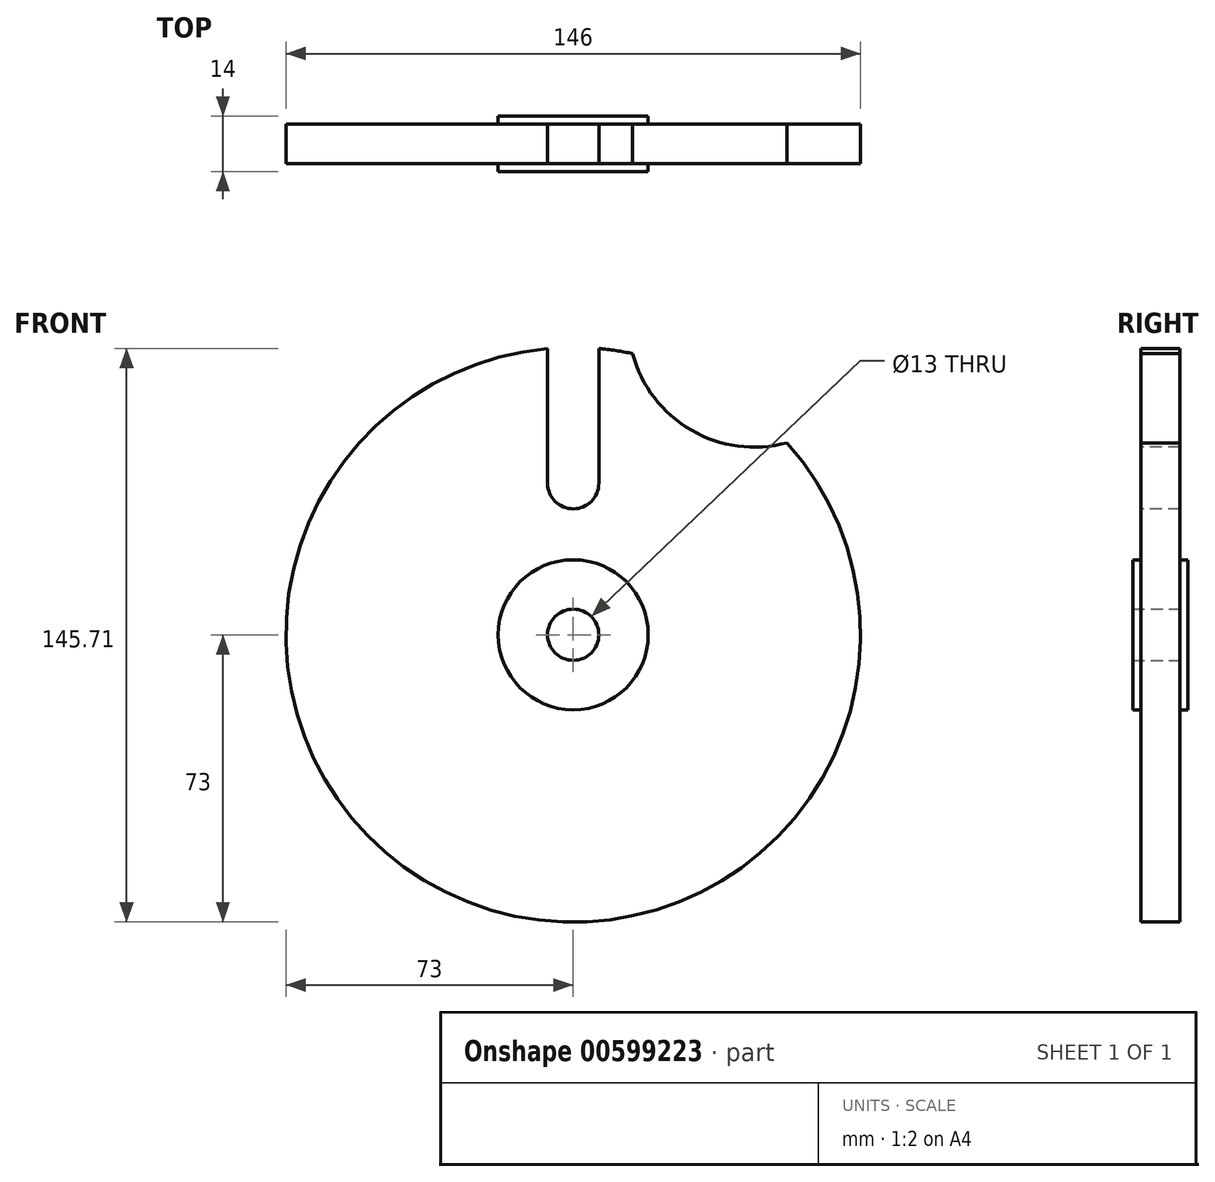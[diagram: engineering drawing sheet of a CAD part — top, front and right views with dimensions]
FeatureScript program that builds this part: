
annotation { "Feature Type Name" : "Feature", "Feature Type Description" : "" }
export const myFeature = defineFeature(function(context is Context, id is Id, definition is map)
    precondition{}
    {
        {
            var Q0;
            Q0=qCreatedBy(makeId("Front.planeOp"),FACE);
            var sketch = newSketch(context, id + "F0", { "sketchPlane" : qUnion([Q0])});
            skCircle(sketch, "E0", {"center": v(0, 92) * mm, "radius": 6.35 * mm, "construction": true});
            skCircle(sketch, "E1", {"center": v(0, 92) * mm, "radius": 31.75 * mm, "construction": true});
            skCircle(sketch, "E2", {"center": v(0, 0) * mm, "radius": 73 * mm, "construction": true});
            skLineSegment(sketch, "E3", {"start": v(0, 0) * mm, "end": v(36.5, 63.22) * mm, "construction": true});
            skCircle(sketch, "E4", {"center": v(0, 38.5) * mm, "radius": 6.35 * mm, "construction": true});
            skSolve(sketch);
        }
        {
            var Q0;
            Q0=qCreatedBy(makeId("Front.planeOp"),FACE);
            var sketch = newSketch(context, id + "F1", { "sketchPlane" : qUnion([Q0])});
            skCircle(sketch, "E5", {"center": v(0, 0) * mm, "radius": 73 * mm});
            skSolve(sketch);
        }
        {
            var Q0;
            Q0 = qSketchRegion(id + "F1", true);
            extrude(context, id + "F2", {"entities" : qUnion([Q0]), "endBound" : BoundingType.SYMMETRIC, "depth" : 10 * mm, "offsetDistance" : 25 * mm});
        }
        {
            var Q0;
            Q0=qCreatedBy(makeId("Front.planeOp"),FACE);
            var sketch = newSketch(context, id + "F3", { "sketchPlane" : qUnion([Q0])});
            skArc(sketch, "E6", {"start": v(-6.5, 38.5) * mm, "mid": v(0, 32) * mm, "end": v(6.5, 38.5) * mm});
            skLineSegment(sketch, "E7", {"start": v(-6.5, 38.5) * mm, "end": v(-6.5, 95.54) * mm});
            skLineSegment(sketch, "E8", {"start": v(-6.5, 95.54) * mm, "end": v(6.5, 95.54) * mm});
            skLineSegment(sketch, "E9", {"start": v(6.5, 38.5) * mm, "end": v(6.5, 95.54) * mm});
            skSolve(sketch);
        }
        {
            var Q0;
            Q0 = qSketchRegion(id + "F3", true);
            extrude(context, id + "F4", {"entities" : qUnion([Q0]), "operationType" : NewBodyOperationType.REMOVE, "endBound" : BoundingType.THROUGH_ALL, "oppositeDirection" : true, "depth" : 25 * mm, "offsetDistance" : 25 * mm, "hasSecondDirection" : true, "secondDirectionBound" : SecondDirectionBoundingType.THROUGH_ALL, "secondDirectionOppositeDirection" : false, "secondDirectionDepth" : 25 * mm});
        }
        {
            var Q0;
            Q0=qCreatedBy(makeId("Right.planeOp"),FACE);
            var sketch = newSketch(context, id + "F5", { "sketchPlane" : qUnion([Q0])});
            skLineSegment(sketch, "E10", {"start": v(10, 0) * mm, "end": v(-10, 0) * mm, "construction": true});
            skSolve(sketch);
        }
        {
            var Q0;
            Q0=qCreatedBy(makeId("Front.planeOp"),FACE);
            var sketch = newSketch(context, id + "F6", { "sketchPlane" : qUnion([Q0])});
            skCircle(sketch, "E11", {"center": v(0, 0) * mm, "radius": 92 * mm, "construction": true});
            skCircle(sketch, "E12", {"center": v(46, 79.67) * mm, "radius": 32 * mm});
            skSolve(sketch);
        }
        {
            var Q0;
            Q0 = qSketchRegion(id + "F6", true);
            extrude(context, id + "F7", {"entities" : qUnion([Q0]), "operationType" : NewBodyOperationType.REMOVE, "endBound" : BoundingType.THROUGH_ALL, "oppositeDirection" : true, "depth" : 25 * mm, "offsetDistance" : 25 * mm, "hasSecondDirection" : true, "secondDirectionBound" : SecondDirectionBoundingType.THROUGH_ALL, "secondDirectionOppositeDirection" : false, "secondDirectionDepth" : 25 * mm});
        }
        {
            var Q0;
            Q0=qCreatedBy(makeId("Front.planeOp"),FACE);
            var sketch = newSketch(context, id + "F8", { "sketchPlane" : qUnion([Q0])});
            skCircle(sketch, "E13", {"center": v(0, 0) * mm, "radius": 19.05 * mm});
            skSolve(sketch);
        }
        {
            var Q0;
            Q0 = qSketchRegion(id + "F8", true);
            extrude(context, id + "F9", {"entities" : qUnion([Q0]), "operationType" : NewBodyOperationType.ADD, "endBound" : BoundingType.SYMMETRIC, "depth" : 14 * mm, "offsetDistance" : 25 * mm});
        }
        {
            var Q0;
            Q0=makeQuery(id+"F9.opExtrude","CAP_FACE",FACE,{"disambiguationData":[OSD([sQuery(id+"F8.wireOp",EDGE,"E13")])],"isStart":true});
            var sketch = newSketch(context, id + "F10", { "sketchPlane" : qUnion([Q0])});
            skCircle(sketch, "E14", {"center": v(0, 0) * mm, "radius": 6.5 * mm});
            skSolve(sketch);
        }
        {
            var Q0;
            Q0 = qSketchRegion(id + "F10", true);
            extrude(context, id + "F11", {"entities" : qUnion([Q0]), "operationType" : NewBodyOperationType.REMOVE, "endBound" : BoundingType.THROUGH_ALL, "oppositeDirection" : true, "depth" : 25 * mm, "offsetDistance" : 25 * mm});
        }
    });
